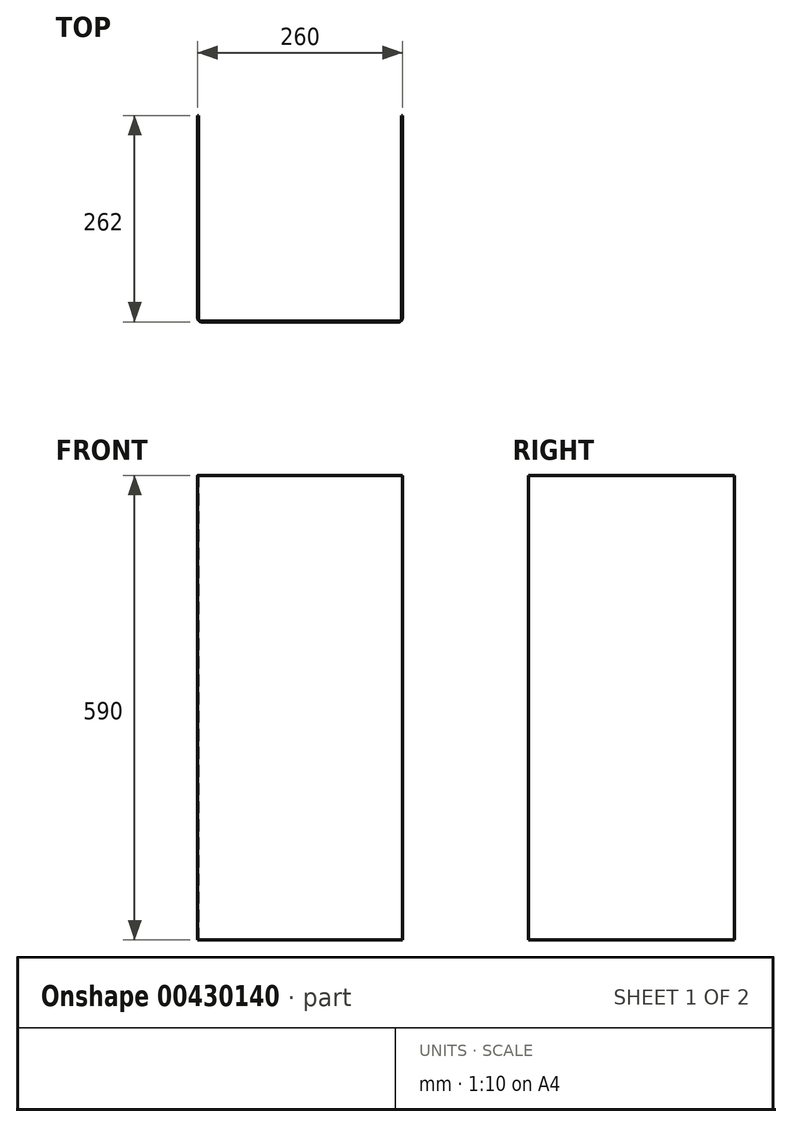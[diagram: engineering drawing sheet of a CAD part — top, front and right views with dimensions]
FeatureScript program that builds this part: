
annotation { "Feature Type Name" : "Feature", "Feature Type Description" : "" }
export const myFeature = defineFeature(function(context is Context, id is Id, definition is map)
    precondition{}
    {
        {
            var Q0;
            Q0=qCreatedBy(makeId("Top.planeOp"),FACE);
            var sketch = newSketch(context, id + "F0", { "sketchPlane" : qUnion([Q0])});
            skLineSegment(sketch, "E0.bottom", {"start": v(0, 0) * mm, "end": v(60.59, 0) * mm});
            skLineSegment(sketch, "E0.top", {"start": v(0, -39.38) * mm, "end": v(60.59, -39.38) * mm});
            skLineSegment(sketch, "E0.left", {"start": v(0, 0) * mm, "end": v(0, -39.38) * mm});
            skLineSegment(sketch, "E0.right", {"start": v(60.59, 0) * mm, "end": v(60.59, -39.38) * mm});
            skSolve(sketch);
        }
        {
            var Q0;
            Q0=makeQuery(id+"F0.imprint","IMPRINT",FACE,{"disambiguationData":[TD([[makeQuery(id+"F0.imprint","IMPRINT",EDGE,{"derivedFrom":sQuery(id+"F0.wireOp",EDGE,"E0.bottom")}),-1.0]])]});
            extrude(context, id + "F1", {"entities" : qUnion([Q0]), "depth" : 590 * mm});
        }
        {
            var Q0;
            Q0=makeQuery(id+"F1.opExtrude","SWEPT_FACE",FACE,{"disambiguationData":[OSD([sQuery(id+"F0.wireOp",EDGE,"E0.left")])]});
            extrude(context, id + "F2", {"entities" : qUnion([Q0]), "operationType" : NewBodyOperationType.ADD, "oppositeDirection" : true, "depth" : 260 * mm});
        }
        {
            var Q0;
            {var subQ0=sQuery(id+"F0.wireOp",EDGE,"E0.bottom");Q0=makeQuery(id+"F2.boolean.opBoolean","MERGE",FACE,{"derivedFrom":[makeQuery(id+"F1.opExtrude","SWEPT_FACE",FACE,{"disambiguationData":[OSD([subQ0])]}),makeQuery(id+"F2.opExtrude","SWEPT_FACE",FACE,{"disambiguationData":[OSD([subQ0,sQuery(id+"F0.wireOp",EDGE,"E0.left")])]})]});}
            extrude(context, id + "F3", {"entities" : qUnion([Q0]), "operationType" : NewBodyOperationType.ADD, "oppositeDirection" : true, "depth" : 262 * mm});
        }
        {
            var Q0;
            {var subQ0=sQuery(id+"F0.wireOp",EDGE,"E0.left");var subQ1=sQuery(id+"F0.wireOp",EDGE,"E0.bottom");Q0=makeQuery(id+"F3.opExtrude","CAP_EDGE",EDGE,{"disambiguationData":[OSD([subQ1,subQ0]),TDD([makeQuery(id+"F1.opExtrude","SWEPT_EDGE",EDGE,{"disambiguationData":[OSD([subQ1,subQ0])]})])],"isStart":false});}
            var Q1;
            {var subQ0=sQuery(id+"F0.wireOp",EDGE,"E0.left");var subQ1=sQuery(id+"F0.wireOp",EDGE,"E0.bottom");Q1=makeQuery(id+"F3.opExtrude","CAP_EDGE",EDGE,{"disambiguationData":[OSD([subQ1,subQ0]),TDD([makeQuery(id+"F2.opExtrude","CAP_EDGE",EDGE,{"disambiguationData":[OSD([subQ1,subQ0])],"isStart":false})])],"isStart":false});}
            fillet(context, id + "F4", {"entities" : qUnion([Q0, Q1]), "radius" : 5 * mm, "tangentPropagation" : true, "allowEdgeOverflow" : false});
        }
        {
            var Q0;
            {var subQ0=sQuery(id+"F0.wireOp",EDGE,"E0.left");var subQ1=sQuery(id+"F0.wireOp",EDGE,"E0.bottom");Q0=makeQuery(id+"F3.boolean.opBoolean","MERGE",FACE,{"derivedFrom":[makeQuery(id+"F2.boolean.opBoolean","MERGE",FACE,{"derivedFrom":[makeQuery(id+"F1.opExtrude","CAP_FACE",FACE,{"disambiguationData":[OSD([subQ1,sQuery(id+"F0.wireOp",EDGE,"E0.top"),subQ0,sQuery(id+"F0.wireOp",EDGE,"E0.right")])],"isStart":false}),makeQuery(id+"F2.opExtrude","SWEPT_FACE",FACE,{"disambiguationData":[OSD([subQ0]),TDD([makeQuery(id+"F1.opExtrude","CAP_EDGE",EDGE,{"disambiguationData":[OSD([subQ0])],"isStart":false})])]})]}),makeQuery(id+"F3.opExtrude","SWEPT_FACE",FACE,{"disambiguationData":[OSD([subQ1,subQ0]),TDD([makeQuery(id+"F2.boolean.opBoolean","MERGE",EDGE,{"derivedFrom":[makeQuery(id+"F1.opExtrude","CAP_EDGE",EDGE,{"disambiguationData":[OSD([subQ1])],"isStart":false}),makeQuery(id+"F2.opExtrude","SWEPT_EDGE",EDGE,{"disambiguationData":[OSD([subQ1,subQ0]),TDD([makeQuery(id+"F1.opExtrude","CAP_VERTEX",VERTEX,{"disambiguationData":[OSD([subQ1,subQ0])],"isStart":false})])]})]})])]})]});}
            var Q1;
            {var subQ0=sQuery(id+"F0.wireOp",EDGE,"E0.bottom");Q1=makeQuery(id+"F2.boolean.opBoolean","MERGE",FACE,{"derivedFrom":[makeQuery(id+"F1.opExtrude","SWEPT_FACE",FACE,{"disambiguationData":[OSD([subQ0])]}),makeQuery(id+"F2.opExtrude","SWEPT_FACE",FACE,{"disambiguationData":[OSD([subQ0,sQuery(id+"F0.wireOp",EDGE,"E0.left")])]})]});}
            var Q2;
            {var subQ0=sQuery(id+"F0.wireOp",EDGE,"E0.left");var subQ1=sQuery(id+"F0.wireOp",EDGE,"E0.bottom");Q2=makeQuery(id+"F3.boolean.opBoolean","MERGE",FACE,{"derivedFrom":[makeQuery(id+"F2.boolean.opBoolean","MERGE",FACE,{"derivedFrom":[makeQuery(id+"F1.opExtrude","CAP_FACE",FACE,{"disambiguationData":[OSD([subQ1,sQuery(id+"F0.wireOp",EDGE,"E0.top"),subQ0,sQuery(id+"F0.wireOp",EDGE,"E0.right")])],"isStart":true}),makeQuery(id+"F2.opExtrude","SWEPT_FACE",FACE,{"disambiguationData":[OSD([subQ0]),TDD([makeQuery(id+"F1.opExtrude","CAP_EDGE",EDGE,{"disambiguationData":[OSD([subQ0])],"isStart":true})])]})]}),makeQuery(id+"F3.opExtrude","SWEPT_FACE",FACE,{"disambiguationData":[OSD([subQ1,subQ0]),TDD([makeQuery(id+"F2.boolean.opBoolean","MERGE",EDGE,{"derivedFrom":[makeQuery(id+"F1.opExtrude","CAP_EDGE",EDGE,{"disambiguationData":[OSD([subQ1])],"isStart":true}),makeQuery(id+"F2.opExtrude","SWEPT_EDGE",EDGE,{"disambiguationData":[OSD([subQ1,subQ0]),TDD([makeQuery(id+"F1.opExtrude","CAP_VERTEX",VERTEX,{"disambiguationData":[OSD([subQ1,subQ0])],"isStart":true})])]})]})])]})]});}
            shell(context, id + "F5", {"entities" : qUnion([Q0, Q1, Q2]), "thickness" : 1 * mm});
        }
    });
